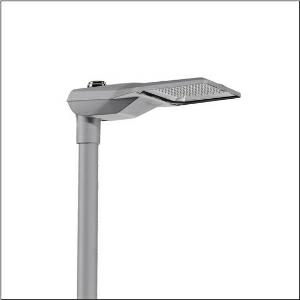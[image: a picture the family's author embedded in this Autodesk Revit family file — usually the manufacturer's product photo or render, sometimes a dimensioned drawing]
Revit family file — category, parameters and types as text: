
# Revit family: streetlight_sl_21_midi___st0_5a_5xe7b47n08nb_57a0
name_source: partatom
category: Lighting Fixtures
units: mm (PartAtom-declared; Revit-internal decimal feet)

## family parameters
Cut with Voids When Loaded = No
Host = Face
Light Source = No
Part Type = Normal
Room Calculation Point = No
Round Connector Dimension = Use Diameter
Shared = No

## types (1)
- --- (1 x LED, 23710 lm, 151.2 W, 4000K)
    Apparent Load = 151 VA
    CIE Flux Codes = 43 76 97 100 100
    Color Rendering = 70
    Color Temperature = 4000K
    Default Elevation = 1800 mm
    Description = Streetlight SL 21 midi, mast luminaire, primary light control with lens, of PMMA, primary optical cover: cover, of toughened safety glass, transparent, light distribution: ST0.5a, light emission: direct distribution, primary light characteristic: asymmetric, installation type: side-entry, LED, 3G 2.5mm², High Power LED, rated luminous flux: 23.710lm, luminous efficacy: 157lm/W, light colour: 740, colour temperature: 4000K, control gear: NEMA (7pin), control: overheat protection, pre-setting: linear dimming characteristic, constant luminous flux control, time-dependent luminous flux control, flexible luminous flux parameterisation, mains connection: 220..240V, AC, 50/60Hz, connection cable pre-assembled, cable length: 12,5m, wiring characteristics: H05VV-F, start of lifetime: 151W, end of service life: 157W, reduction: 70W, luminaire housing, of diecast aluminium (EN AC-44300), powder-coated, SITECO metallic grey (DB 702S), corrosivity category C5 high according to DIN EN ISO 12944, multi-level sealing system, sealing non-destructively replaceable, inclination adjustable: 0°, 5°, 10°, 15°, length: 644mm, width: 335mm, height: 110mm, spigot size: 42mm (side-entry), mounting height: 4..8m, protection rating (complete): IP66, insulation class (complete): insulation class I (protective earthing), certification: CE, ENEC, ENEC+, VDE, impact resistance: IK10, permissible operating ambient temperature for outdoor applications: -40..+50°C, standard-compliant lighting for roads and squares, packaging unit: 1 piece

Light Distribution: ST0.5a
    Height = 111 mm
    Lamp = 1 x LED
    Lamp Light Flux = 23710 lm
    Lamp Power = 151.2 W
    Lamp count = 1
    Length = 644 mm
    Luminous efficacy = 157 lm/W
    Manufacturer = Siteco
    ModVariant = No
    Model = 5XE7B47N08NB
    Number of Poles = 1
    OnlyDefault = Yes
    Power Factor = 1
    Product Name = Streetlight SL 21 midi | ST0.5a
    Product group = mast luminaire | pylon top
    ProductGroupID = 6100
    Protection Class = Protection class I
    Protection Degree = IP 66
    RLX_Detail_Level = 1
    RLX_Emergency_Light_Flux = 0 lm
    RLX_Emergency_Type = 0
    RLX_Emergency_Type_DB = No
    RlxData = <blob elided: 37713 chars, md5=a02273f0>
    Socket = socket
    Standby Power = 0 W
    System Light Flux = 23710 lm
    System Power = 151 W
    Type Comments = factory setting: luminous flux: 100 % | dim-lin: 254 | 802 mA
    Type Image = l_1294377.jpg
    URL = http://relux.com
    VarID = @adj_136149
    Voltage = 0 V
    Weight = 0.00 kg
    Width = 336 mm

## geometry (parser evidence)
native form markers: Blend x4, Sweep x11
no freeform markers — native parametric forms only
